# Revit family: Haworth_Alodia_Stool
name_source: partatom
category: Furniture
revit_build: Autodesk Revit 2018 (Build: 20170223_1515(x64)
units: mm (PartAtom-declared; Revit-internal decimal feet)

## family parameters
Always vertical = Yes
Cut with Voids When Loaded = No
OmniClass Number = 23.40.70.14.64.21
OmniClass Title = Systems Furniture
Room Calculation Point = No
Shared = No
Work Plane-Based = No

## types (2) — shared parameters
Actual Depth = 18"
Actual Width = 21 1/4"
Assembly Code = E2020200
Bar Height = 11 193/256"
Base Depth Top = 9"
Base Width Bottom = 15 3/4"
Base Width Top = 14"
Description = Haworth Alodia Stool
Foot Bar Straight = 11 83/128"
Manufacturer = Haworth
Model = HCCE-AL
Revision Number = 4
Size = Verify Final Dim. w/ Haworth
URL = http://www.haworth.com
URL - Product = http://www.haworth.com
Warranty = http://www.haworth.com

## per-type parameters (varying)
| type | Actual Height | High | Low |
| HCCE-AL - High | 31 1/2" | Yes | No |
| HCCE-AL - Low | 27 1/2" | No | Yes |

## geometry (parser evidence)
native form markers: Sweep x3
no freeform markers — native parametric forms only
